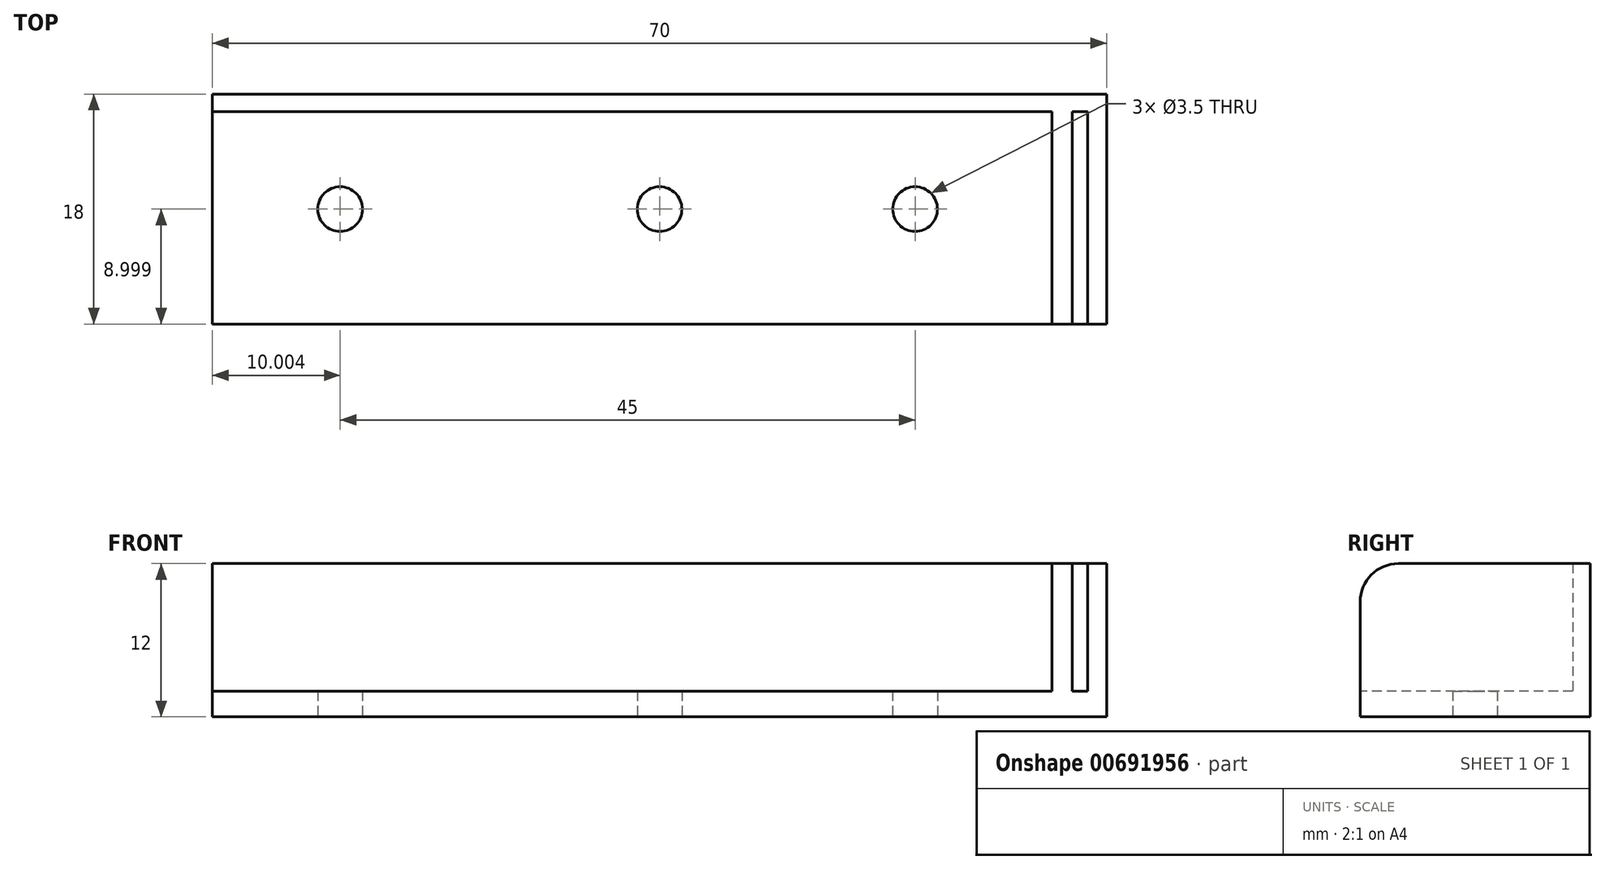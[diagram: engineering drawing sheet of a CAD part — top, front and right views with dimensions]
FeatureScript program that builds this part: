
annotation { "Feature Type Name" : "Feature", "Feature Type Description" : "" }
export const myFeature = defineFeature(function(context is Context, id is Id, definition is map)
    precondition{}
    {
        {
            var Q0;
            Q0=qCreatedBy(makeId("Top.planeOp"),FACE);
            var sketch = newSketch(context, id + "F0", { "sketchPlane" : qUnion([Q0])});
            skLineSegment(sketch, "E0.bottom", {"start": v(-20.29, -7.8) * mm, "end": v(49.71, -7.8) * mm});
            skLineSegment(sketch, "E0.top", {"start": v(-20.29, -25.8) * mm, "end": v(49.71, -25.8) * mm});
            skLineSegment(sketch, "E0.left", {"start": v(-20.29, -7.8) * mm, "end": v(-20.29, -25.8) * mm});
            skLineSegment(sketch, "E0.right", {"start": v(49.71, -7.8) * mm, "end": v(49.71, -25.8) * mm});
            skLineSegment(sketch, "E1", {"start": v(-20.29, -9.15) * mm, "end": v(49.71, -9.15) * mm});
            skLineSegment(sketch, "E2", {"start": v(48.21, -9.15) * mm, "end": v(48.21, -25.8) * mm});
            skLineSegment(sketch, "E3", {"start": v(47.01, -25.8) * mm, "end": v(47.01, -9.15) * mm});
            skLineSegment(sketch, "E4", {"start": v(45.41, -25.8) * mm, "end": v(45.41, -9.15) * mm});
            skPoint(sketch, "E5", {"position": v(-20.29, -16.8) * mm});
            skCircle(sketch, "E6", {"center": v(34.71, -16.8) * mm, "radius": 1.75 * mm});
            skCircle(sketch, "E7", {"center": v(14.71, -16.8) * mm, "radius": 1.75 * mm});
            skCircle(sketch, "E8", {"center": v(-10.29, -16.8) * mm, "radius": 1.75 * mm});
            skSolve(sketch);
        }
        {
            var Q0;
            {var subQ5=sQuery(id+"F0.wireOp",EDGE,"E0.bottom");Q0=makeQuery(id+"F0.imprint","IMPRINT",FACE,{"disambiguationData":[TD([[makeQuery(id+"F0.imprint","IMPRINT",EDGE,{"derivedFrom":subQ5}),-1.0]])]});}
            var Q1;
            {var subQ3=sQuery(id+"F0.wireOp",EDGE,"E2");Q1=makeQuery(id+"F0.imprint","IMPRINT",FACE,{"disambiguationData":[TD([[makeQuery(id+"F0.imprint","IMPRINT",EDGE,{"derivedFrom":subQ3}),1.0]])]});}
            var Q2;
            {var subQ0=sQuery(id+"F0.wireOp",EDGE,"E3");Q2=makeQuery(id+"F0.imprint","IMPRINT",FACE,{"disambiguationData":[TD([[makeQuery(id+"F0.imprint","IMPRINT",EDGE,{"derivedFrom":subQ0}),1.0]])]});}
            extrude(context, id + "F1", {"entities" : qUnion([Q0, Q1, Q2]), "depth" : 12 * mm, "offsetDistance" : 25 * mm});
        }
        {
            var Q0;
            {var subQ0=sQuery(id+"F0.wireOp",EDGE,"E4");Q0=makeQuery(id+"F0.imprint","IMPRINT",FACE,{"disambiguationData":[TD([[makeQuery(id+"F0.imprint","IMPRINT",EDGE,{"derivedFrom":subQ0}),1.0]])]});}
            var Q1;
            {var subQ0=sQuery(id+"F0.wireOp",EDGE,"E2");Q1=makeQuery(id+"F0.imprint","IMPRINT",FACE,{"disambiguationData":[TD([[makeQuery(id+"F0.imprint","IMPRINT",EDGE,{"derivedFrom":subQ0}),-1.0]])]});}
            extrude(context, id + "F2", {"entities" : qUnion([Q0, Q1]), "operationType" : NewBodyOperationType.ADD, "depth" : 2 * mm, "offsetDistance" : 25 * mm});
        }
        {
            var Q0;
            {var subQ0=sQuery(id+"F0.wireOp",EDGE,"E0.top");Q0=makeQuery(id+"F1.opExtrude","CAP_EDGE",EDGE,{"disambiguationData":[OSD([subQ0]),TDD([makeQuery(id+"F0.imprint","IMPRINT",EDGE,{"disambiguationData":[TD([[makeQuery(id+"F0.imprint","INTERSECT",VERTEX,{"derivedFrom":[subQ0,sQuery(id+"F0.wireOp",EDGE,"E0.right")]}),1.0]])],"derivedFrom":subQ0})])],"isStart":false});}
            var Q1;
            {var subQ0=sQuery(id+"F0.wireOp",EDGE,"E0.top");Q1=makeQuery(id+"F1.opExtrude","CAP_EDGE",EDGE,{"disambiguationData":[OSD([subQ0]),TDD([makeQuery(id+"F0.imprint","IMPRINT",EDGE,{"disambiguationData":[TD([[makeQuery(id+"F0.imprint","INTERSECT",VERTEX,{"derivedFrom":[subQ0,sQuery(id+"F0.wireOp",EDGE,"E3")]}),1.0]])],"derivedFrom":subQ0})])],"isStart":false});}
            fillet(context, id + "F3", {"entities" : qUnion([Q0, Q1]), "radius" : 3 * mm, "tangentPropagation" : true, "allowEdgeOverflow" : false});
        }
    });
